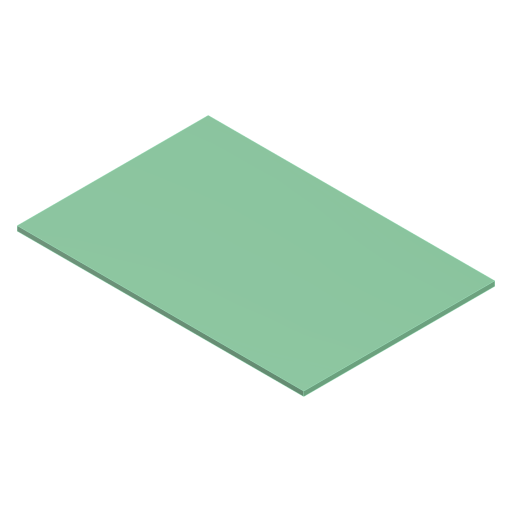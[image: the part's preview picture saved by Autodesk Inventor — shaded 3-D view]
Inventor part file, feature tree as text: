
AUTODESK INVENTOR PART (.ipt)
format: ipt  version: 2023 (Build 270158000, 158)  size: 99,328 bytes
history: native  units: in
note: dims shown in document units (in); Inventor stores cm internally (conversion verified against a paired STEP export)
features: extrude x2, sketch x2, other x1
ambient origin geometry x8: Origin, YZ Plane, XZ Plane, XY Plane, X Axis, Y Axis, Z Axis, Center Point
bodies: Body1 (feature_tree)
feature tree (5):
  other  "ソリッド1"
  extrude  "押し出し1"  Depth=0.9843in
  extrude  "押し出し2"  Depth=39.3701in
  sketch  "スケッチ1"
  sketch  "スケッチ2"
